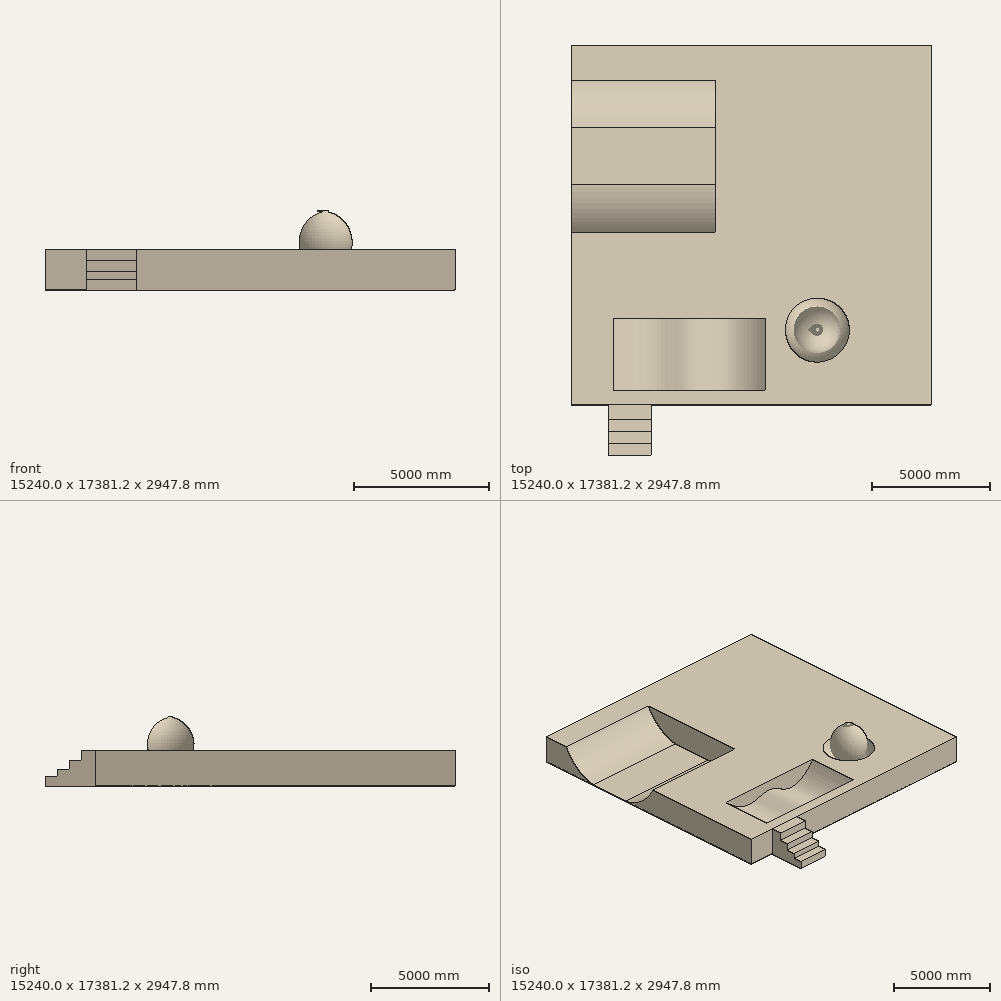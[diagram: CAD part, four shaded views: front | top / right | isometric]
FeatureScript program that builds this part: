
annotation { "Feature Type Name" : "Feature", "Feature Type Description" : "" }
export const myFeature = defineFeature(function(context is Context, id is Id, definition is map)
    precondition{}
    {
        {
            var Q0;
            Q0=qCreatedBy(makeId("Top.planeOp"),FACE);
            var sketch = newSketch(context, id + "F0", { "sketchPlane" : qUnion([Q0])});
            skLineSegment(sketch, "E0.bottom", {"start": v(0, 0) * mm, "end": v(15240, 0) * mm});
            skLineSegment(sketch, "E0.top", {"start": v(0, 15240) * mm, "end": v(15240, 15240) * mm});
            skLineSegment(sketch, "E0.left", {"start": v(0, 0) * mm, "end": v(0, 15240) * mm});
            skLineSegment(sketch, "E0.right", {"start": v(15240, 0) * mm, "end": v(15240, 15240) * mm});
            skLineSegment(sketch, "E1.bottom", {"start": v(15240, 15240) * mm, "end": v(8833.37, 15240) * mm});
            skLineSegment(sketch, "E1.top", {"start": v(15240, 15240) * mm, "end": v(8833.37, 15240) * mm});
            skLineSegment(sketch, "E1.left", {"start": v(15240, 15240) * mm, "end": v(15240, 15240) * mm});
            skLineSegment(sketch, "E1.right", {"start": v(8833.37, 15240) * mm, "end": v(8833.37, 15240) * mm});
            skSolve(sketch);
        }
        {
            var Q0;
            Q0=makeQuery(id+"F0.imprint","IMPRINT",FACE,{"disambiguationData":[TD([[makeQuery(id+"F0.imprint","IMPRINT",EDGE,{"derivedFrom":sQuery(id+"F0.wireOp",EDGE,"E0.bottom")}),1.0]])]});
            extrude(context, id + "F1", {"entities" : qUnion([Q0]), "depth" : 1524 * mm});
        }
        {
            var Q0;
            Q0=makeQuery(id+"F0.imprint","IMPRINT",FACE,{"disambiguationData":[TD([[makeQuery(id+"F0.imprint","IMPRINT",EDGE,{"derivedFrom":sQuery(id+"F0.wireOp",EDGE,"E0.bottom")}),1.0]])]});
            extrude(context, id + "F2", {"entities" : qUnion([Q0]), "depth" : 30.48 * mm});
        }
        {
            var Q0;
            Q0=makeQuery(id+"F1.opExtrude","SWEPT_FACE",FACE,{"disambiguationData":[OSD([sQuery(id+"F0.wireOp",EDGE,"E0.bottom")])]});
            var sketch = newSketch(context, id + "F3", { "sketchPlane" : qUnion([Q0])});
            skFitSpline(sketch, "E2", {"points": [v(1766.2, 1524) * mm, v(2729.25, 906.23) * mm, v(3813.85, 737.93) * mm, v(5001.3, 990.38) * mm, v(5973.7, 644.42) * mm, v(6768.45, 485.47) * mm, v(7675.4, 915.58) * mm, v(8217.7, 1524) * mm], "startDerivative": vector(6115.8, -4583.84) * mm, "endDerivative": vector(3663.6, 4921.68) * mm});
            skLineSegment(sketch, "E3", {"start": v(1766.2, 1524) * mm, "end": v(8217.7, 1524) * mm});
            skSolve(sketch);
        }
        {
            var Q0;
            Q0=makeQuery(id+"F3.imprint","IMPRINT",FACE,{"disambiguationData":[TD([[makeQuery(id+"F3.imprint","IMPRINT",EDGE,{"derivedFrom":sQuery(id+"F3.wireOp",EDGE,"E2")}),1.0]])]});
            extrude(context, id + "F4", {"entities" : qUnion([Q0]), "depth" : 3048 * mm});
        }
        {
            var Q0;
            Q0=makeQuery(id+"F4.opExtrude","SWEPT_BODY",BODY,{"disambiguationData":[OSD([sQuery(id+"F3.wireOp",EDGE,"E2"),sQuery(id+"F3.wireOp",EDGE,"E3")])]});
            transform(context, id + "F5", {"entities" : qUnion([Q0]), "transformType" : TransformType.TRANSLATION_3D, "dx" : 0 * mm, "dy" : 3657.6 * mm, "dz" : 0 * mm, "makeCopy" : false});
        }
        {
            var Q0;
            Q0=makeQuery(id+"F4.opExtrude","SWEPT_BODY",BODY,{"disambiguationData":[OSD([sQuery(id+"F3.wireOp",EDGE,"E2"),sQuery(id+"F3.wireOp",EDGE,"E3")])]});
            var Q1;
            Q1=makeQuery(id+"F1.opExtrude","SWEPT_BODY",BODY,{"disambiguationData":[OSD([sQuery(id+"F0.wireOp",EDGE,"E0.bottom"),sQuery(id+"F0.wireOp",EDGE,"E0.top"),sQuery(id+"F0.wireOp",EDGE,"E0.left"),sQuery(id+"F0.wireOp",EDGE,"E0.right"),sQuery(id+"F0.wireOp",EDGE,"E1.top")])]});
            booleanBodies(context, id + "F6", {"operationType" : BooleanOperationType.SUBTRACTION, "tools" : qUnion([Q0]), "targets" : qUnion([Q1])});
        }
        {
            var Q0;
            Q0=makeQuery(id+"F1.opExtrude","SWEPT_FACE",FACE,{"disambiguationData":[OSD([sQuery(id+"F0.wireOp",EDGE,"E0.bottom")])]});
            var sketch = newSketch(context, id + "F7", { "sketchPlane" : qUnion([Q0])});
            skArc(sketch, "E4", {"start": v(9059.2, 1524) * mm, "mid": v(9550.27, 787.43) * mm, "end": v(10414.95, 597.67) * mm});
            skLineSegment(sketch, "E5", {"start": v(10414.95, 597.67) * mm, "end": v(10414.95, 1524) * mm});
            skLineSegment(sketch, "E6", {"start": v(10414.95, 1524) * mm, "end": v(9059.2, 1524) * mm});
            skSolve(sketch);
        }
        {
            var Q0;
            Q0=makeQuery(id+"F7.imprint","IMPRINT",FACE,{"disambiguationData":[TD([[makeQuery(id+"F7.imprint","IMPRINT",EDGE,{"derivedFrom":sQuery(id+"F7.wireOp",EDGE,"E4")}),1.0]])]});
            var Q1;
            Q1=sQuery(id+"F7.wireOp",EDGE,"E5");
            revolve(context, id + "F8", {"entities" : qUnion([Q0]), "axis" : qUnion([Q1]), "revolveType" : RevolveType.FULL});
        }
        {
            var Q0;
            Q0=makeQuery(id+"F8.opRevolve","SWEPT_BODY",BODY,{"disambiguationData":[OSD([sQuery(id+"F7.wireOp",EDGE,"E4"),sQuery(id+"F7.wireOp",EDGE,"E5"),sQuery(id+"F7.wireOp",EDGE,"E6")])]});
            transform(context, id + "F9", {"entities" : qUnion([Q0]), "transformType" : TransformType.TRANSLATION_3D, "dx" : 0 * mm, "dy" : 3169.92 * mm, "dz" : 0 * mm, "makeCopy" : false});
        }
        {
            var Q0;
            Q0=makeQuery(id+"F8.opRevolve","SWEPT_BODY",BODY,{"disambiguationData":[OSD([sQuery(id+"F7.wireOp",EDGE,"E4"),sQuery(id+"F7.wireOp",EDGE,"E5"),sQuery(id+"F7.wireOp",EDGE,"E6")])]});
            var Q1;
            Q1=makeQuery(id+"F1.opExtrude","SWEPT_BODY",BODY,{"disambiguationData":[OSD([sQuery(id+"F0.wireOp",EDGE,"E0.bottom"),sQuery(id+"F0.wireOp",EDGE,"E0.top"),sQuery(id+"F0.wireOp",EDGE,"E0.left"),sQuery(id+"F0.wireOp",EDGE,"E0.right"),sQuery(id+"F0.wireOp",EDGE,"E1.top")])]});
            booleanBodies(context, id + "F10", {"operationType" : BooleanOperationType.SUBTRACTION, "tools" : qUnion([Q0]), "targets" : qUnion([Q1])});
        }
        {
            var Q0;
            Q0=makeQuery(id+"F1.opExtrude","SWEPT_FACE",FACE,{"disambiguationData":[OSD([sQuery(id+"F0.wireOp",EDGE,"E0.bottom")])]});
            var sketch = newSketch(context, id + "F11", { "sketchPlane" : qUnion([Q0])});
            skLineSegment(sketch, "E7", {"start": v(1541.8, 1524) * mm, "end": v(2177.6, 1524) * mm});
            skLineSegment(sketch, "E8", {"start": v(2177.6, 1524) * mm, "end": v(2177.6, 1083.88) * mm});
            skLineSegment(sketch, "E9", {"start": v(2177.6, 1083.88) * mm, "end": v(2673.15, 1083.88) * mm});
            skLineSegment(sketch, "E10", {"start": v(2673.15, 1083.88) * mm, "end": v(2673.15, 700.52) * mm});
            skLineSegment(sketch, "E11", {"start": v(2673.15, 700.52) * mm, "end": v(3178.05, 700.52) * mm});
            skLineSegment(sketch, "E12", {"start": v(3178.05, 700.52) * mm, "end": v(3178.05, 410.67) * mm});
            skLineSegment(sketch, "E13", {"start": v(3178.05, 410.67) * mm, "end": v(3682.95, 410.67) * mm});
            skLineSegment(sketch, "E14", {"start": v(3682.95, 410.67) * mm, "end": v(3682.95, 0) * mm});
            skLineSegment(sketch, "E15", {"start": v(3682.95, 0) * mm, "end": v(1541.8, 0) * mm});
            skLineSegment(sketch, "E16", {"start": v(1541.8, 0) * mm, "end": v(1541.8, 1524) * mm});
            skSolve(sketch);
        }
        {
            var Q0;
            Q0=makeQuery(id+"F11.imprint","IMPRINT",FACE,{"disambiguationData":[TD([[makeQuery(id+"F11.imprint","IMPRINT",EDGE,{"derivedFrom":sQuery(id+"F11.wireOp",EDGE,"E7")}),-1.0]])]});
            extrude(context, id + "F12", {"entities" : qUnion([Q0]), "depth" : 1828.8 * mm});
        }
        {
            var Q0;
            Q0=makeQuery(id+"F12.opExtrude","SWEPT_BODY",BODY,{"disambiguationData":[OSD([sQuery(id+"F11.wireOp",EDGE,"E7"),sQuery(id+"F11.wireOp",EDGE,"E8"),sQuery(id+"F11.wireOp",EDGE,"E9"),sQuery(id+"F11.wireOp",EDGE,"E10"),sQuery(id+"F11.wireOp",EDGE,"E11"),sQuery(id+"F11.wireOp",EDGE,"E12"),sQuery(id+"F11.wireOp",EDGE,"E13"),sQuery(id+"F11.wireOp",EDGE,"E14"),sQuery(id+"F11.wireOp",EDGE,"E15"),sQuery(id+"F11.wireOp",EDGE,"E16")])]});
            var Q1;
            Q1=makeQuery(id+"F12.opExtrude","CAP_EDGE",EDGE,{"disambiguationData":[OSD([sQuery(id+"F11.wireOp",EDGE,"E16")])],"isStart":false});
            transform(context, id + "F13", {"entities" : qUnion([Q0]), "transformType" : TransformType.ROTATION, "transformAxis" : qUnion([Q1]), "angle" : 90 * degree, "oppositeDirection" : true, "makeCopy" : false});
        }
        {
            var Q0;
            Q0=makeQuery(id+"F12.opExtrude","SWEPT_BODY",BODY,{"disambiguationData":[OSD([sQuery(id+"F11.wireOp",EDGE,"E7"),sQuery(id+"F11.wireOp",EDGE,"E8"),sQuery(id+"F11.wireOp",EDGE,"E9"),sQuery(id+"F11.wireOp",EDGE,"E10"),sQuery(id+"F11.wireOp",EDGE,"E11"),sQuery(id+"F11.wireOp",EDGE,"E12"),sQuery(id+"F11.wireOp",EDGE,"E13"),sQuery(id+"F11.wireOp",EDGE,"E14"),sQuery(id+"F11.wireOp",EDGE,"E15"),sQuery(id+"F11.wireOp",EDGE,"E16")])]});
            transform(context, id + "F14", {"entities" : qUnion([Q0]), "transformType" : TransformType.TRANSLATION_3D, "dx" : 0 * mm, "dy" : 1828.8 * mm, "dz" : 0 * mm, "makeCopy" : false});
        }
        {
            var Q0;
            Q0=makeQuery(id+"F1.opExtrude","SWEPT_FACE",FACE,{"disambiguationData":[OSD([sQuery(id+"F0.wireOp",EDGE,"E0.left")])]});
            var sketch = newSketch(context, id + "F15", { "sketchPlane" : qUnion([Q0])});
            skArc(sketch, "E17", {"start": v(-13764.62, 1524) * mm, "mid": v(-12838.56, 468.78) * mm, "end": v(-11515.18, 0) * mm});
            skLineSegment(sketch, "E18", {"start": v(-11515.18, 0) * mm, "end": v(-9732.6, 0) * mm});
            skArc(sketch, "E19", {"start": v(-9732.6, 0) * mm, "mid": v(-8302.99, 412.76) * mm, "end": v(-7313.39, 1524) * mm});
            skLineSegment(sketch, "E20", {"start": v(-13764.62, 1524) * mm, "end": v(-7313.39, 1524) * mm});
            skSolve(sketch);
        }
        {
            var Q0;
            Q0=makeQuery(id+"F15.imprint","IMPRINT",FACE,{"disambiguationData":[TD([[makeQuery(id+"F15.imprint","IMPRINT",EDGE,{"derivedFrom":sQuery(id+"F15.wireOp",EDGE,"E17")}),1.0]])]});
            extrude(context, id + "F16", {"entities" : qUnion([Q0]), "depth" : 6096 * mm});
        }
        {
            var Q0;
            Q0=makeQuery(id+"F16.opExtrude","SWEPT_BODY",BODY,{"disambiguationData":[OSD([sQuery(id+"F15.wireOp",EDGE,"E17"),sQuery(id+"F15.wireOp",EDGE,"E18"),sQuery(id+"F15.wireOp",EDGE,"E19"),sQuery(id+"F15.wireOp",EDGE,"E20")])]});
            transform(context, id + "F17", {"entities" : qUnion([Q0]), "transformType" : TransformType.TRANSLATION_3D, "dx" : 6096 * mm, "dy" : 0 * mm, "dz" : 0 * mm, "makeCopy" : false});
        }
        {
            var Q0;
            Q0=makeQuery(id+"F16.opExtrude","SWEPT_BODY",BODY,{"disambiguationData":[OSD([sQuery(id+"F15.wireOp",EDGE,"E17"),sQuery(id+"F15.wireOp",EDGE,"E18"),sQuery(id+"F15.wireOp",EDGE,"E19"),sQuery(id+"F15.wireOp",EDGE,"E20")])]});
            var Q1;
            Q1=makeQuery(id+"F1.opExtrude","SWEPT_BODY",BODY,{"disambiguationData":[OSD([sQuery(id+"F0.wireOp",EDGE,"E0.bottom"),sQuery(id+"F0.wireOp",EDGE,"E0.top"),sQuery(id+"F0.wireOp",EDGE,"E0.left"),sQuery(id+"F0.wireOp",EDGE,"E0.right"),sQuery(id+"F0.wireOp",EDGE,"E1.top")])]});
            booleanBodies(context, id + "F18", {"operationType" : BooleanOperationType.SUBTRACTION, "tools" : qUnion([Q0]), "targets" : qUnion([Q1])});
        }
    });
